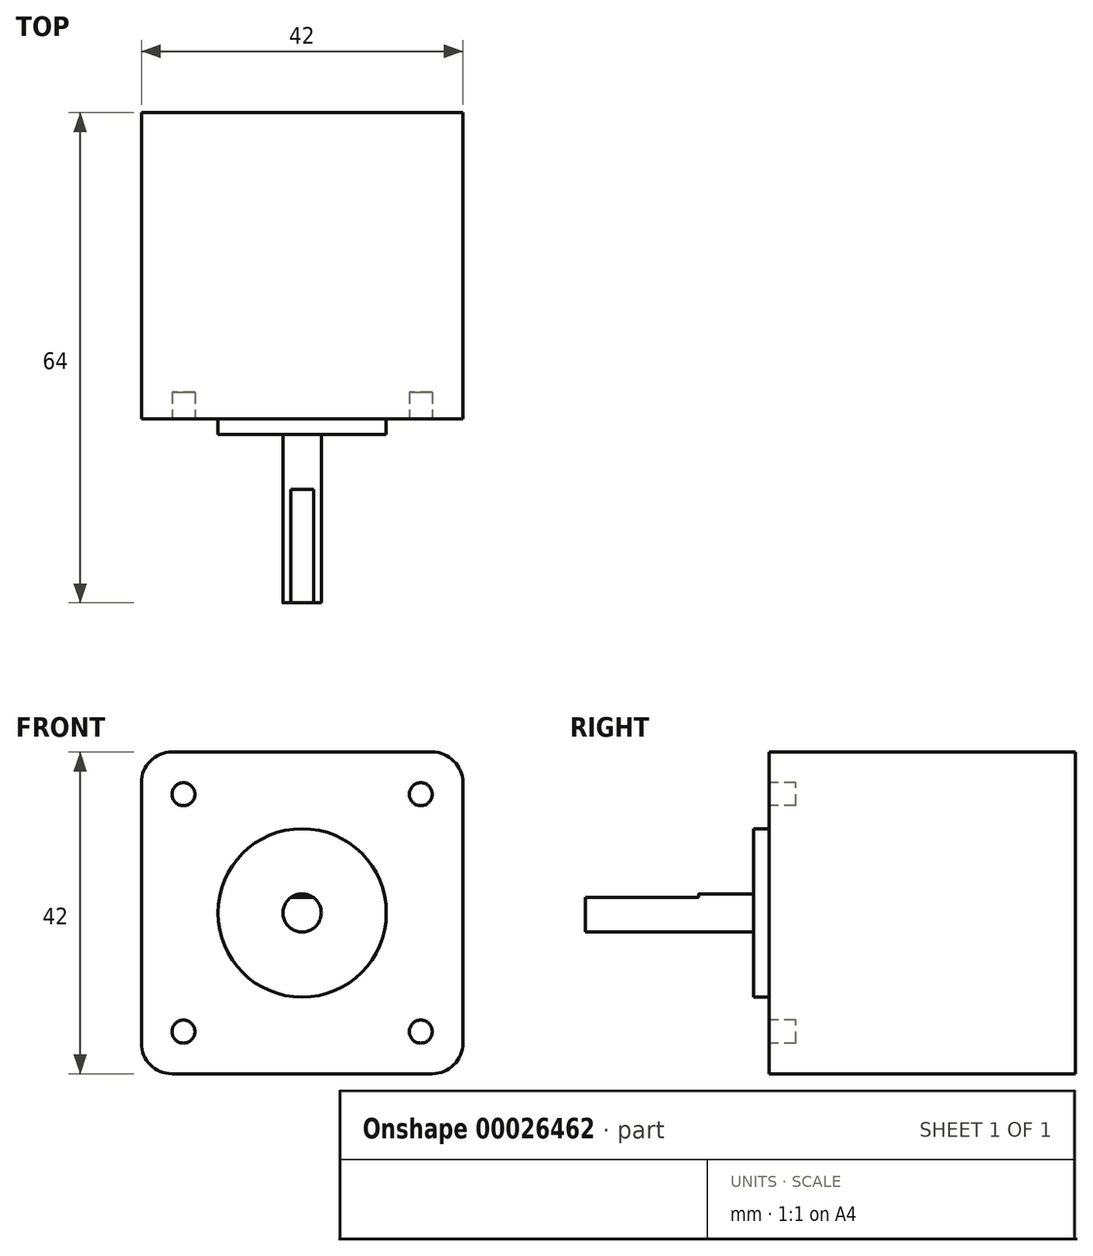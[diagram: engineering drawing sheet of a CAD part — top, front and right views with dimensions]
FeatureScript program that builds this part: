
annotation { "Feature Type Name" : "Feature", "Feature Type Description" : "" }
export const myFeature = defineFeature(function(context is Context, id is Id, definition is map)
    precondition{}
    {
        {
            var Q0;
            Q0=qCreatedBy(makeId("Front.planeOp"),FACE);
            var sketch = newSketch(context, id + "F0", { "sketchPlane" : qUnion([Q0])});
            skLineSegment(sketch, "E0.rect.bottom", {"start": v(-17, 21) * mm, "end": v(17, 21) * mm});
            skLineSegment(sketch, "E0.rect.top", {"start": v(-17, -21) * mm, "end": v(17, -21) * mm});
            skLineSegment(sketch, "E0.rect.left", {"start": v(-21, 17) * mm, "end": v(-21, -17) * mm});
            skLineSegment(sketch, "E0.rect.right", {"start": v(21, 17) * mm, "end": v(21, -17) * mm});
            skPoint(sketch, "E0.rect.middle", {"position": v(0, 0) * mm});
            skLineSegment(sketch, "E1.rect.bottom", {"start": v(-15.5, 15.5) * mm, "end": v(15.5, 15.5) * mm, "construction": true});
            skLineSegment(sketch, "E1.rect.top", {"start": v(-15.5, -15.5) * mm, "end": v(15.5, -15.5) * mm, "construction": true});
            skLineSegment(sketch, "E1.rect.left", {"start": v(-15.5, 15.5) * mm, "end": v(-15.5, -15.5) * mm, "construction": true});
            skLineSegment(sketch, "E1.rect.right", {"start": v(15.5, 15.5) * mm, "end": v(15.5, -15.5) * mm, "construction": true});
            skCircle(sketch, "E2", {"center": v(-15.5, 15.5) * mm, "radius": 1.5 * mm});
            skCircle(sketch, "E3", {"center": v(15.5, 15.5) * mm, "radius": 1.5 * mm});
            skCircle(sketch, "E4", {"center": v(-15.5, -15.5) * mm, "radius": 1.5 * mm});
            skCircle(sketch, "E5", {"center": v(15.5, -15.5) * mm, "radius": 1.5 * mm});
            skCircle(sketch, "E6", {"center": v(0, 0) * mm, "radius": 11 * mm});
            skCircle(sketch, "E7", {"center": v(0, 0) * mm, "radius": 2.5 * mm});
            skPoint(sketch, "E8.visualSharp", {"position": v(-21, 21) * mm});
            skArc(sketch, "E8.filletArc", {"start": v(-17, 21) * mm, "mid": v(-19.83, 19.83) * mm, "end": v(-21, 17) * mm});
            skPoint(sketch, "E9.visualSharp", {"position": v(21, 21) * mm});
            skArc(sketch, "E9.filletArc", {"start": v(21, 17) * mm, "mid": v(19.83, 19.83) * mm, "end": v(17, 21) * mm});
            skPoint(sketch, "E10.visualSharp", {"position": v(21, -21) * mm});
            skArc(sketch, "E10.filletArc", {"start": v(17, -21) * mm, "mid": v(19.83, -19.83) * mm, "end": v(21, -17) * mm});
            skPoint(sketch, "E11.visualSharp", {"position": v(-21, -21) * mm});
            skArc(sketch, "E11.filletArc", {"start": v(-21, -17) * mm, "mid": v(-19.83, -19.83) * mm, "end": v(-17, -21) * mm});
            skSolve(sketch);
        }
        {
            var Q0;
            Q0=makeQuery(id+"F0.imprint","IMPRINT",FACE,{"disambiguationData":[TD([[makeQuery(id+"F0.imprint","IMPRINT",EDGE,{"derivedFrom":sQuery(id+"F0.wireOp",EDGE,"E2")}),1.0]])]});
            var Q1;
            Q1=makeQuery(id+"F0.imprint","IMPRINT",FACE,{"disambiguationData":[TD([[makeQuery(id+"F0.imprint","IMPRINT",EDGE,{"derivedFrom":sQuery(id+"F0.wireOp",EDGE,"E3")}),1.0]])]});
            var Q2;
            Q2=makeQuery(id+"F0.imprint","IMPRINT",FACE,{"disambiguationData":[TD([[makeQuery(id+"F0.imprint","IMPRINT",EDGE,{"derivedFrom":sQuery(id+"F0.wireOp",EDGE,"E4")}),1.0]])]});
            var Q3;
            Q3=makeQuery(id+"F0.imprint","IMPRINT",FACE,{"disambiguationData":[TD([[makeQuery(id+"F0.imprint","IMPRINT",EDGE,{"derivedFrom":sQuery(id+"F0.wireOp",EDGE,"E5")}),1.0]])]});
            var Q4;
            Q4=makeQuery(id+"F0.imprint","IMPRINT",FACE,{"disambiguationData":[TD([[makeQuery(id+"F0.imprint","IMPRINT",EDGE,{"derivedFrom":sQuery(id+"F0.wireOp",EDGE,"E7")}),1.0]])]});
            var Q5;
            Q5=makeQuery(id+"F0.imprint","IMPRINT",FACE,{"disambiguationData":[TD([[makeQuery(id+"F0.imprint","IMPRINT",EDGE,{"derivedFrom":sQuery(id+"F0.wireOp",EDGE,"E6")}),1.0]])]});
            var Q6;
            Q6=makeQuery(id+"F0.imprint","IMPRINT",FACE,{"disambiguationData":[TD([[makeQuery(id+"F0.imprint","IMPRINT",EDGE,{"derivedFrom":sQuery(id+"F0.wireOp",EDGE,"E0.rect.bottom")}),-1.0]])]});
            extrude(context, id + "F1", {"entities" : qUnion([Q0, Q1, Q2, Q3, Q4, Q5, Q6]), "oppositeDirection" : true, "depth" : 40 * mm});
        }
        {
            var Q0;
            Q0=makeQuery(id+"F0.imprint","IMPRINT",FACE,{"disambiguationData":[TD([[makeQuery(id+"F0.imprint","IMPRINT",EDGE,{"derivedFrom":sQuery(id+"F0.wireOp",EDGE,"E2")}),1.0]])]});
            var Q1;
            Q1=makeQuery(id+"F0.imprint","IMPRINT",FACE,{"disambiguationData":[TD([[makeQuery(id+"F0.imprint","IMPRINT",EDGE,{"derivedFrom":sQuery(id+"F0.wireOp",EDGE,"E3")}),1.0]])]});
            var Q2;
            Q2=makeQuery(id+"F0.imprint","IMPRINT",FACE,{"disambiguationData":[TD([[makeQuery(id+"F0.imprint","IMPRINT",EDGE,{"derivedFrom":sQuery(id+"F0.wireOp",EDGE,"E5")}),1.0]])]});
            var Q3;
            Q3=makeQuery(id+"F0.imprint","IMPRINT",FACE,{"disambiguationData":[TD([[makeQuery(id+"F0.imprint","IMPRINT",EDGE,{"derivedFrom":sQuery(id+"F0.wireOp",EDGE,"E4")}),1.0]])]});
            var Q4;
            Q4=sQuery(id+"F0.wireOp",EDGE,"E2");
            var Q5;
            Q5=sQuery(id+"F0.wireOp",EDGE,"E3");
            var Q6;
            Q6=sQuery(id+"F0.wireOp",EDGE,"E5");
            var Q7;
            Q7=sQuery(id+"F0.wireOp",EDGE,"E4");
            extrude(context, id + "F2", {"entities" : qUnion([Q0, Q1, Q2, Q3]), "operationType" : NewBodyOperationType.REMOVE, "surfaceEntities" : qUnion([Q4, Q5, Q6, Q7]), "oppositeDirection" : true, "depth" : 3.5 * mm});
        }
        {
            var Q0;
            Q0=makeQuery(id+"F0.imprint","IMPRINT",FACE,{"disambiguationData":[TD([[makeQuery(id+"F0.imprint","IMPRINT",EDGE,{"derivedFrom":sQuery(id+"F0.wireOp",EDGE,"E6")}),1.0]])]});
            extrude(context, id + "F3", {"entities" : qUnion([Q0]), "operationType" : NewBodyOperationType.ADD, "depth" : 2 * mm});
        }
        {
            var Q0;
            Q0=makeQuery(id+"F0.imprint","IMPRINT",FACE,{"disambiguationData":[TD([[makeQuery(id+"F0.imprint","IMPRINT",EDGE,{"derivedFrom":sQuery(id+"F0.wireOp",EDGE,"E7")}),1.0]])]});
            var Q1;
            Q1=sQuery(id+"F0.wireOp",EDGE,"E7");
            extrude(context, id + "F4", {"entities" : qUnion([Q0]), "operationType" : NewBodyOperationType.ADD, "surfaceEntities" : qUnion([Q1]), "depth" : 24 * mm});
        }
        {
            var Q0;
            Q0=makeQuery(id+"F1.opExtrude","SWEPT_FACE",FACE,{"disambiguationData":[OSD([sQuery(id+"F0.wireOp",EDGE,"E0.rect.left")])]});
            var sketch = newSketch(context, id + "F5", { "sketchPlane" : qUnion([Q0])});
            skLineSegment(sketch, "E12.bottom", {"start": v(24, 2.5) * mm, "end": v(9.2, 2.5) * mm});
            skLineSegment(sketch, "E12.top", {"start": v(24, 2) * mm, "end": v(9.2, 2) * mm});
            skLineSegment(sketch, "E12.left", {"start": v(24, 2.5) * mm, "end": v(24, 2) * mm});
            skLineSegment(sketch, "E12.right", {"start": v(9.2, 2.5) * mm, "end": v(9.2, 2) * mm});
            skLineSegment(sketch, "E13.0", {"start": v(2, 2.5) * mm, "end": v(2, -2.5) * mm, "construction": true});
            skLineSegment(sketch, "E14", {"start": v(2, 2.5) * mm, "end": v(24, 2.5) * mm, "construction": true});
            skSolve(sketch);
        }
        {
            var Q0;
            Q0=makeQuery(id+"F5.imprint","IMPRINT",FACE,{"disambiguationData":[TD([[makeQuery(id+"F5.imprint","IMPRINT",EDGE,{"derivedFrom":sQuery(id+"F5.wireOp",EDGE,"E12.bottom")}),1.0]])]});
            extrude(context, id + "F6", {"entities" : qUnion([Q0]), "operationType" : NewBodyOperationType.REMOVE, "endBound" : BoundingType.THROUGH_ALL, "oppositeDirection" : true, "depth" : 25 * mm});
        }
    });
